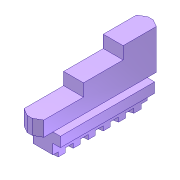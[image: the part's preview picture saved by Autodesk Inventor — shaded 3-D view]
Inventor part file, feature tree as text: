
AUTODESK INVENTOR PART (.ipt)
format: ipt  version: unknown  size: 337,920 bytes
history: native  units: in
note: dims shown in document units (in); Inventor stores cm internally (conversion verified against a paired STEP export)
features: extrude x7, sketch x7, fillet x1, projected_geometry x1
ambient origin geometry x8: Origin, YZ Plane, XZ Plane, XY Plane, X Axis, Y Axis, Z Axis, Center Point
feature tree (16):
  extrude  "Extrusion8"  Depth=0.1378in
  extrude  "Extrusion9"  Depth=0.0787in
  extrude  "Extrusion10"  Depth=0.315in
  extrude  "Extrusion11"  TaperAngle=30.0deg  [1 undecoded]
  extrude  "Extrusion13"  Depth=0.7874in TaperAngle=0.0deg
  extrude  "Extrusion14"  Depth=0.1969in TaperAngle=0.0deg
  fillet  "Fillet1"  Radius=0.315in
  extrude  "Extrusion16"  Depth=0.1181in
  sketch  "Sketch10"  dims[d51=0.0787in d52=0.1378in]
  sketch  "Sketch11"  dims[d53=0.0787in d54=0.0787in]
  sketch  "Sketch12"  dims[d55=0.0787in d56=0.315in]
  sketch  "Sketch13"  dims[d57=0.9843in d58=0.0in d59=30.0deg]
  sketch  "Sketch15"  dims[d60=30.0deg d61=0.7874in d62=0.0in]
  sketch  "Sketch16"  dims[d63=0.315in d64=0.1969in d65=0.0in d66=0.315in]
  sketch  "Sketch18"  dims[d67=0.0984in d68=0.0in d72=0.1181in d73=0.1181in d74=0.0787in d75=0.0in d76=0.3661in d79=0.0551in d81=0.0551in d83=0.0551in d85=0.0551in d87=0.0551in d89=0.0551in d90=0.0354in d91=0.0in d92=0.1181in d93=0.1181in d94=0.1181in d95=0.1181in d96=0.1181in d102=0.0008in d103=0.0118in d104=0.0118in d105=0.3937in d106=0.0in]
  projected_geometry  "Projected Loop1"
note: 1 required parameter value undecoded (feature->parameter linkage not recoverable at this tier; creation-order binding heuristic only, values carry confidence <= 0.55)
